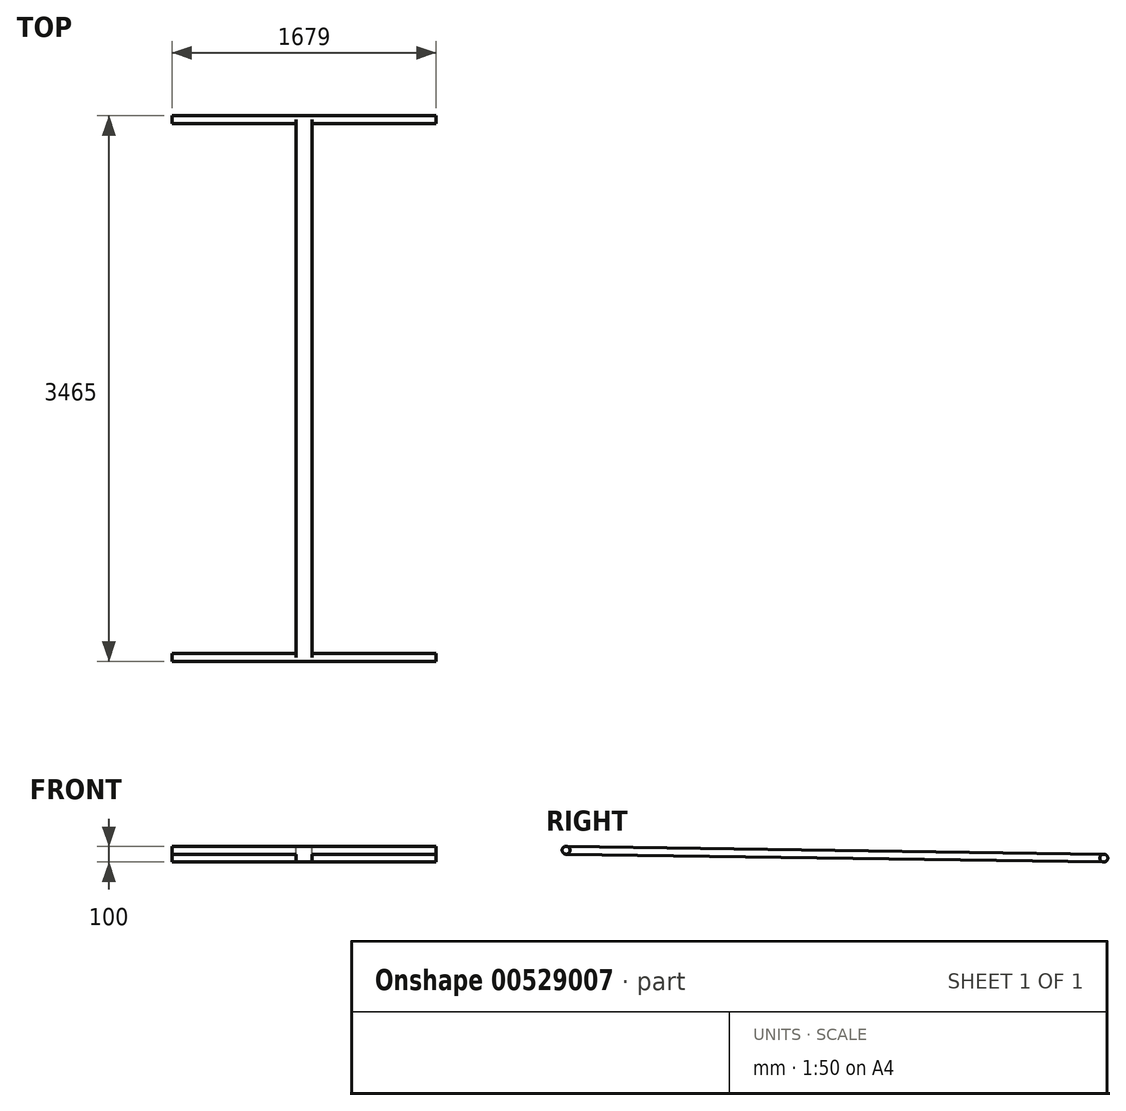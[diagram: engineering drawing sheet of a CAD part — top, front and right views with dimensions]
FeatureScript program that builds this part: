
annotation { "Feature Type Name" : "Feature", "Feature Type Description" : "" }
export const myFeature = defineFeature(function(context is Context, id is Id, definition is map)
    precondition{}
    {
        {
            var Q0;
            Q0=qCreatedBy(makeId("Top.planeOp"),FACE);
            var sketch = newSketch(context, id + "F0", { "sketchPlane" : qUnion([Q0])});
            skLineSegment(sketch, "E0", {"start": v(0, 0) * mm, "end": v(0, 2866) * mm, "construction": true});
            skLineSegment(sketch, "E1", {"start": v(0, 0) * mm, "end": v(0, -549) * mm, "construction": true});
            skLineSegment(sketch, "E2", {"start": v(839.5, -549) * mm, "end": v(-839.5, -549) * mm, "construction": true});
            skLineSegment(sketch, "E3", {"start": v(839.5, 2866) * mm, "end": v(-839.5, 2866) * mm, "construction": true});
            skSolve(sketch);
        }
        {
            var Q0;
            Q0=qCreatedBy(makeId("Right.planeOp"),FACE);
            var Q1;
            Q1=sQuery(id+"F0.wireOp",VERTEX,"E2.start");
            cPlane(context, id + "F1", {"entities" : qUnion([Q0, Q1]), "cplaneType" : CPlaneType.PLANE_POINT, "offset" : 25 * mm, "width" : 150 * mm, "height" : 150 * mm});
        }
        {
            var Q0;
            Q0=qCreatedBy(id+"F1.planeOp",FACE);
            var sketch = newSketch(context, id + "F2", { "sketchPlane" : qUnion([Q0])});
            skLineSegment(sketch, "E4", {"start": v(-549, 50) * mm, "end": v(-549, 0) * mm, "construction": true});
            skCircle(sketch, "E5", {"center": v(-549, 50) * mm, "radius": 25 * mm});
            skCircle(sketch, "E6", {"center": v(2866, 0) * mm, "radius": 25 * mm});
            skSolve(sketch);
        }
        {
            var Q0;
            Q0 = qSketchRegion(id + "F2", true);
            var Q1;
            Q1=sQuery(id+"F0.wireOp",VERTEX,"E2.end");
            extrude(context, id + "F3", {"entities" : qUnion([Q0]), "endBound" : BoundingType.UP_TO_VERTEX, "oppositeDirection" : true, "depth" : 25 * mm, "endBoundEntityVertex" : qUnion([Q1]), "offsetDistance" : 25 * mm});
        }
        {
            var Q0;
            Q0=qCreatedBy(makeId("Right.planeOp"),FACE);
            var sketch = newSketch(context, id + "F4", { "sketchPlane" : qUnion([Q0])});
            skArc(sketch, "E7.0", {"start": v(-548.63, 75) * mm, "mid": v(-574, 50.37) * mm, "end": v(-549.37, 25) * mm});
            skArc(sketch, "E8.0", {"start": v(2865.63, -25) * mm, "mid": v(2891, -0.37) * mm, "end": v(2866.37, 25) * mm});
            skLineSegment(sketch, "E9", {"start": v(2865.63, -25) * mm, "end": v(-549.37, 25) * mm});
            skLineSegment(sketch, "E10", {"start": v(2866.37, 25) * mm, "end": v(-548.63, 75) * mm});
            skSolve(sketch);
        }
        {
            var Q0;
            Q0 = qSketchRegion(id + "F4", true);
            extrude(context, id + "F5", {"entities" : qUnion([Q0]), "operationType" : NewBodyOperationType.ADD, "endBound" : BoundingType.SYMMETRIC, "depth" : 100 * mm, "offsetDistance" : 25 * mm});
        }
    });
